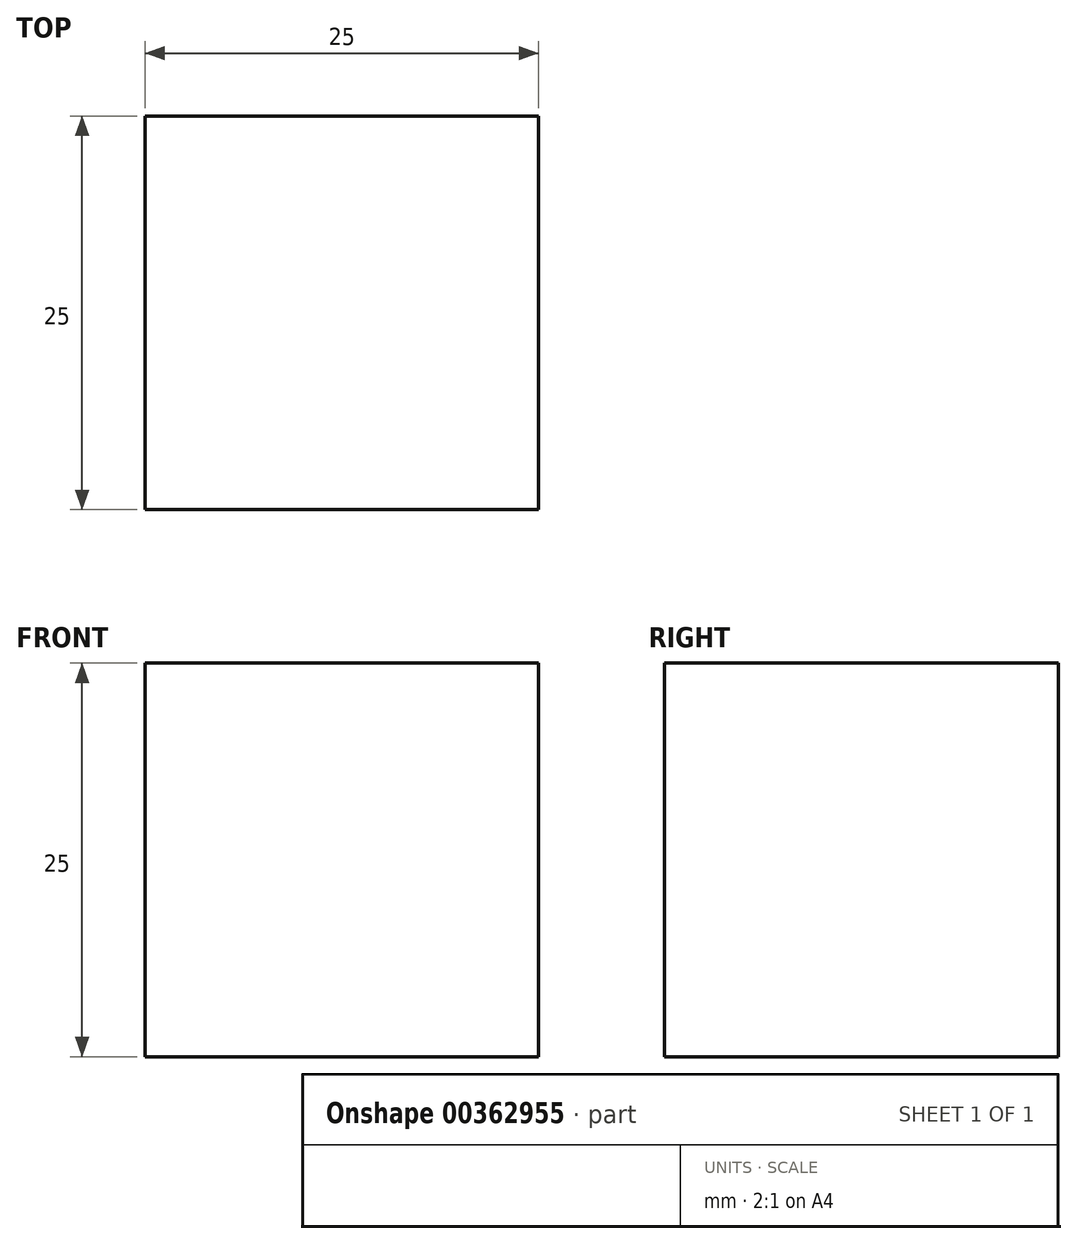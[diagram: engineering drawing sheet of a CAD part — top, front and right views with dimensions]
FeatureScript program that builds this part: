
annotation { "Feature Type Name" : "Feature", "Feature Type Description" : "" }
export const myFeature = defineFeature(function(context is Context, id is Id, definition is map)
    precondition{}
    {
        {
            var Q0;
            Q0=qCreatedBy(makeId("Front.planeOp"),FACE);
            var sketch = newSketch(context, id + "F0", { "sketchPlane" : qUnion([Q0])});
            skLineSegment(sketch, "E0.bottom", {"start": v(-63, 33.41) * mm, "end": v(-38, 33.41) * mm});
            skLineSegment(sketch, "E0.top", {"start": v(-63, 8.41) * mm, "end": v(-38, 8.41) * mm});
            skLineSegment(sketch, "E0.left", {"start": v(-63, 33.41) * mm, "end": v(-63, 8.41) * mm});
            skLineSegment(sketch, "E0.right", {"start": v(-38, 33.41) * mm, "end": v(-38, 8.41) * mm});
            skSolve(sketch);
        }
        {
            var Q0;
            Q0=makeQuery(id+"F0.imprint","IMPRINT",FACE,{"disambiguationData":[TD([[makeQuery(id+"F0.imprint","IMPRINT",EDGE,{"derivedFrom":sQuery(id+"F0.wireOp",EDGE,"E0.bottom")}),-1.0]])]});
            extrude(context, id + "F1", {"entities" : qUnion([Q0]), "depth" : 25 * mm});
        }
    });
